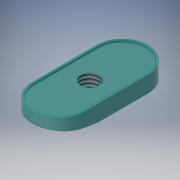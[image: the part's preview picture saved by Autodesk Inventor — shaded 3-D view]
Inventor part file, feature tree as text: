
AUTODESK INVENTOR PART (.ipt)
format: ipt  version: 2018 (Build 220112000, 112)  size: 169,472 bytes
history: native  units: in
note: dims shown in document units (in); Inventor stores cm internally (conversion verified against a paired STEP export)
features: sketch x6, extrude x4, hole x1, thread x1, plane x1, revolve x1
ambient origin geometry x8: Origin, YZ Plane, XZ Plane, XY Plane, X Axis, Y Axis, Z Axis, Center Point
bodies: Solid1 (feature_tree)
feature tree (14):
  extrude  "Extrusion1"  Depth=0.02in TaperAngle=0.0deg
  extrude  "Extrusion2"  Depth=0.25in TaperAngle=0.0deg
  hole  "Hole1"  [1 undecoded]
  thread  "Thread1"  [1 undecoded]
  extrude  "Extrusion3"  Depth=0.18in
  plane  "Work Plane1"
  revolve  "Revolution1"  [1 undecoded]
  extrude  "Extrusion4"  Depth=0.05in
  sketch  "Sketch1"  dims[d3=0.22in d4=0.0in d8=0.02in d9=0.0in]
  sketch  "Sketch2"  dims[d10=0.25in]
  sketch  "Sketch3"  dims[d11=0.25in d12=0.75in d13=0.375in d14=0.25in d15=0.5635in d16=1.0in d17=0.8108in d18=1.0in d19=0.0in]
  sketch  "Sketch4"  dims[d20=0.02in d21=0.0in d22=0.1in d23=0.5in]
  sketch  "Sketch5"  dims[d24=90.0deg d25=0.18in]
  sketch  "Sketch6"  dims[d26=0.4375in d27=0.05in d28=0.0in d29=0.0618in d30=0.24in d31=0.54in]
note: 3 required parameter values undecoded (feature->parameter linkage not recoverable at this tier; creation-order binding heuristic only, values carry confidence <= 0.55)